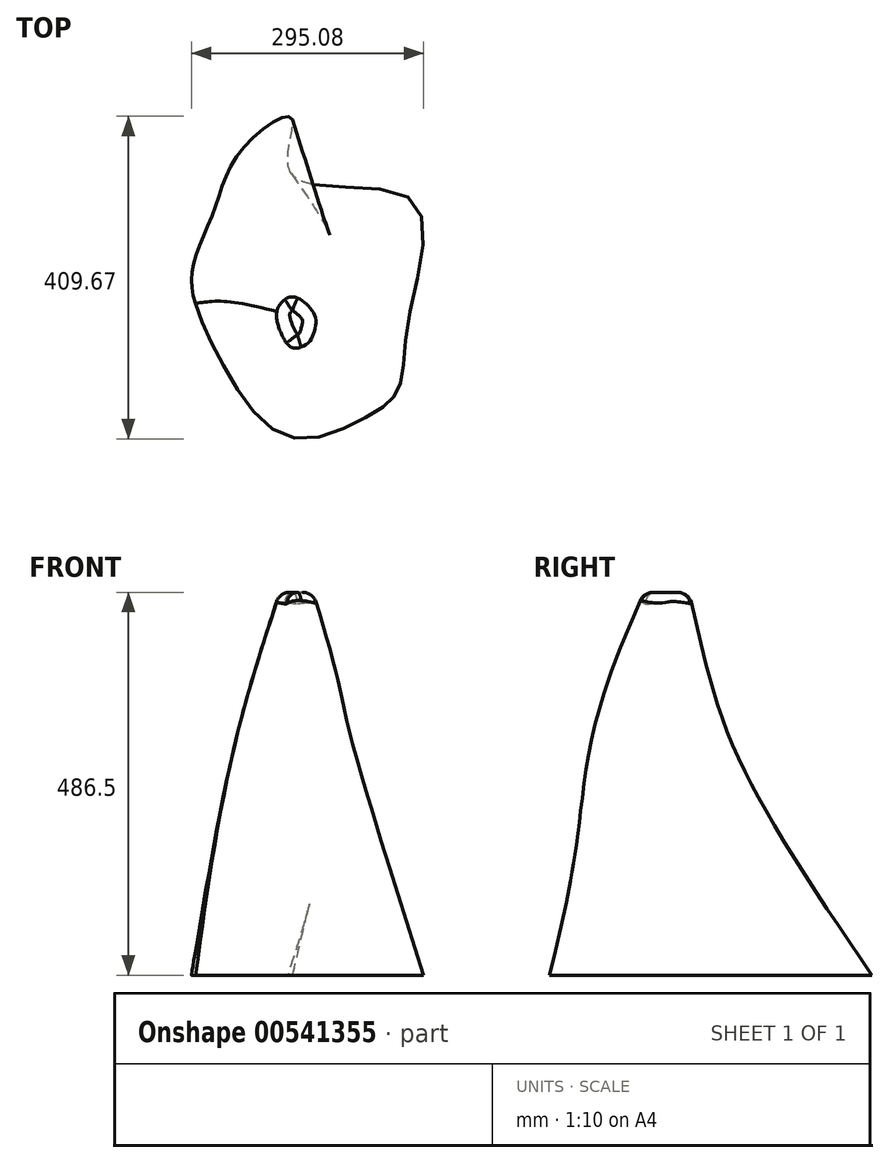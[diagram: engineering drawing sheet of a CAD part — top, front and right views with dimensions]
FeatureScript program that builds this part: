
annotation { "Feature Type Name" : "Feature", "Feature Type Description" : "" }
export const myFeature = defineFeature(function(context is Context, id is Id, definition is map)
    precondition{}
    {
        {
            var Q0;
            Q0=qCreatedBy(makeId("Top.planeOp"),FACE);
            var sketch = newSketch(context, id + "F0", { "sketchPlane" : qUnion([Q0])});
            skFitSpline(sketch, "E0", {"points": [v(-122.03, 19.22) * mm, v(-82.4, -67.45) * mm, v(0, -151.18) * mm, v(101.85, -121.2) * mm, v(135.61, -89.48) * mm, v(148.82, 0) * mm, v(150.52, 152.5) * mm, v(0, 183.6) * mm, v(0, 254.77) * mm, v(-61.1, 217.52) * mm, v(-98.54, 137.46) * mm, v(-125.7, 65.49) * mm, v(-122.03, 19.22) * mm]});
            skSolve(sketch);
        }
        {
            var Q0;
            Q0=makeQuery(id+"F0.imprint","IMPRINT",FACE,{"disambiguationData":[TD([[makeQuery(id+"F0.imprint","IMPRINT",EDGE,{"derivedFrom":sQuery(id+"F0.wireOp",EDGE,"E0")}),1.0]])]});
            cPlane(context, id + "F1", {"entities" : qUnion([Q0]), "cplaneType" : CPlaneType.OFFSET, "offset" : 332.83 * mm, "width" : 152.4 * mm, "height" : 152.4 * mm});
        }
        {
            var Q0;
            Q0=qCreatedBy(id+"F1.planeOp",FACE);
            var sketch = newSketch(context, id + "F2", { "sketchPlane" : qUnion([Q0])});
            skFitSpline(sketch, "E1", {"points": [v(0, 64.12) * mm, v(58.78, 47.63) * mm, v(67.01, 0) * mm, v(37.15, -89.4) * mm, v(-32.86, -44.06) * mm, v(-59.63, 32.18) * mm, v(0, 64.12) * mm]});
            skSolve(sketch);
        }
        {
            var Q0;
            Q0=qCreatedBy(id+"F1.planeOp",FACE);
            cPlane(context, id + "F3", {"entities" : qUnion([Q0]), "cplaneType" : CPlaneType.OFFSET, "offset" : 153.67 * mm, "width" : 152.4 * mm, "height" : 152.4 * mm});
        }
        {
            var Q0;
            Q0=qCreatedBy(id+"F3.planeOp",FACE);
            var sketch = newSketch(context, id + "F4", { "sketchPlane" : qUnion([Q0])});
            skPoint(sketch, "E2.0.internal.orphan", {"position": v(0, 11.8) * mm});
            skPoint(sketch, "E2.3.internal.orphan", {"position": v(0, -22.14) * mm});
            skFitSpline(sketch, "E3", {"points": [v(-12.87, -10.88) * mm, v(-14.37, 9.98) * mm, v(0, 24.44) * mm, v(12.48, 19.53) * mm, v(24.74, 4.26) * mm, v(27.06, -8.28) * mm, v(25.1, -17.25) * mm, v(17.25, -28.58) * mm, v(0, -32.44) * mm, v(-8.22, -23.43) * mm, v(-12.87, -10.88) * mm]});
            skSolve(sketch);
        }
        {
            var Q0;
            Q0 = qSketchRegion(id + "F0", true);
            var Q1;
            Q1 = qSketchRegion(id + "F2", true);
            var Q2;
            Q2 = qSketchRegion(id + "F4", true);
            loft(context, id + "F5", {"sheetProfilesArray" : [{ "sheetProfileEntities" : qUnion([Q0]) }, { "sheetProfileEntities" : qUnion([Q1]) }, { "sheetProfileEntities" : qUnion([Q2]) }]});
        }
        {
            var Q0;
            Q0=makeQuery(id+"F5.opLoft","MID_CAP_EDGE",EDGE,{"disambiguationData":[OSD([sQuery(id+"F0.wireOp",EDGE,"E0"),sQuery(id+"F4.wireOp",EDGE,"E3")])],"capPos":2.0});
            fillet(context, id + "F6", {"entities" : qUnion([Q0]), "radius" : 17.78 * mm, "tangentPropagation" : true, "allowEdgeOverflow" : false});
        }
    });
